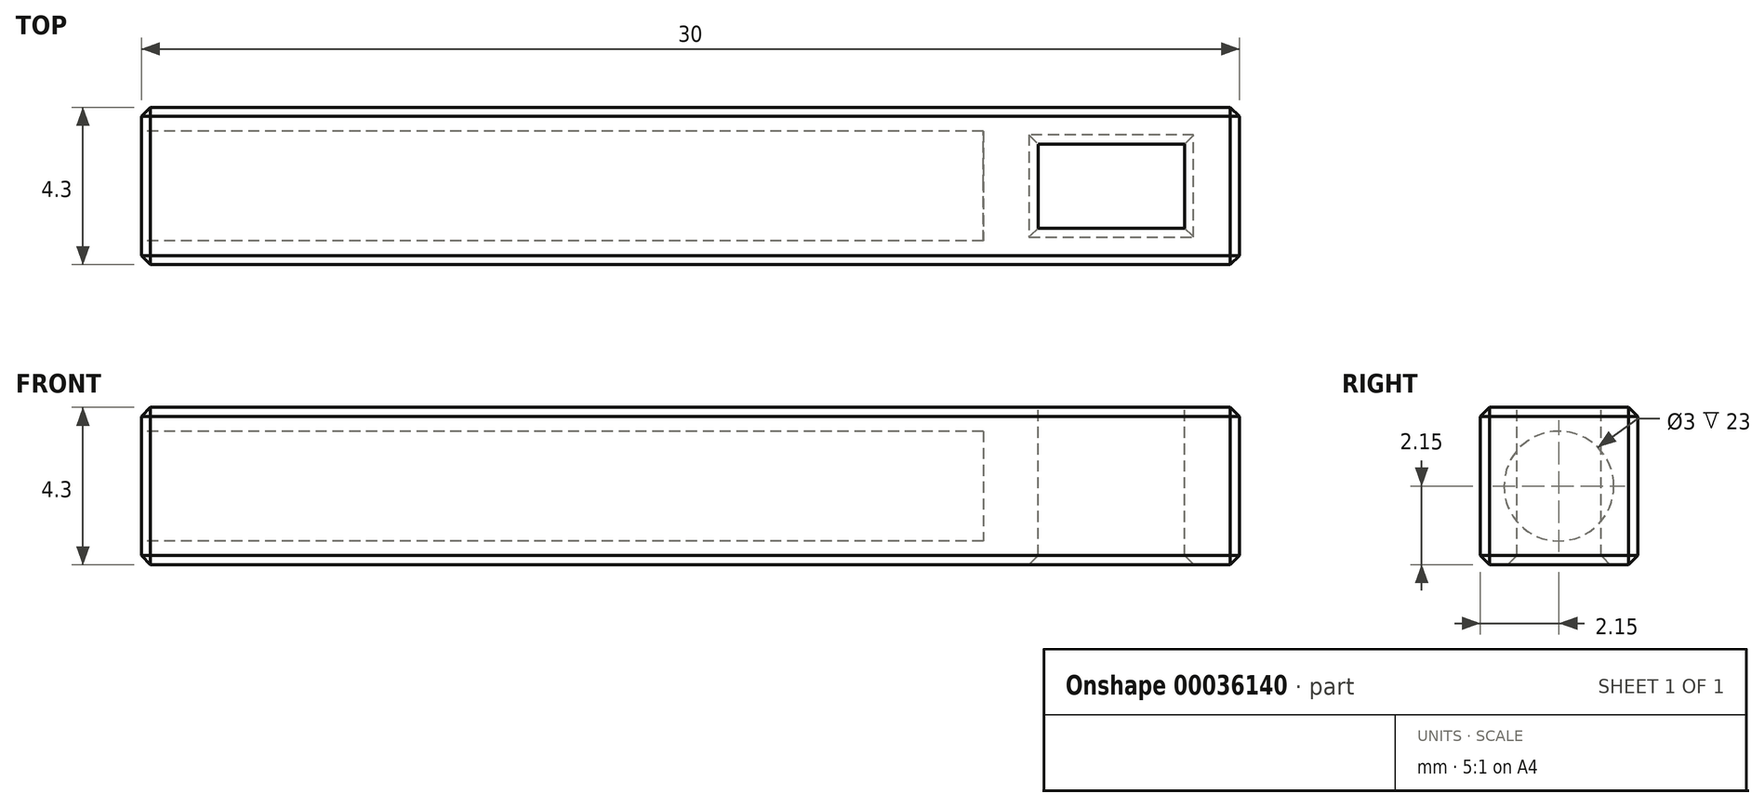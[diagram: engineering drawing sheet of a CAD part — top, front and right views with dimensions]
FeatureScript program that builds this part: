
annotation { "Feature Type Name" : "Feature", "Feature Type Description" : "" }
export const myFeature = defineFeature(function(context is Context, id is Id, definition is map)
    precondition{}
    {
        {
            var Q0;
            Q0=qCreatedBy(makeId("Top.planeOp"),FACE);
            var sketch = newSketch(context, id + "F0", { "sketchPlane" : qUnion([Q0])});
            skLineSegment(sketch, "E0.bottom", {"start": v(-16.76, 4.3) * mm, "end": v(13.24, 4.3) * mm});
            skLineSegment(sketch, "E0.top", {"start": v(-16.76, 0) * mm, "end": v(13.24, 0) * mm});
            skLineSegment(sketch, "E0.left", {"start": v(-16.76, 4.3) * mm, "end": v(-16.76, 0) * mm});
            skLineSegment(sketch, "E0.right", {"start": v(13.24, 4.3) * mm, "end": v(13.24, 0) * mm});
            skSolve(sketch);
        }
        {
            var Q0;
            Q0 = qSketchRegion(id + "F0", true);
            extrude(context, id + "F1", {"entities" : qUnion([Q0]), "depth" : 4.3 * mm});
        }
        {
            var Q0;
            Q0=makeQuery(id+"F1.opExtrude","CAP_FACE",FACE,{"disambiguationData":[OSD([sQuery(id+"F0.wireOp",EDGE,"E0.bottom"),sQuery(id+"F0.wireOp",EDGE,"E0.top"),sQuery(id+"F0.wireOp",EDGE,"E0.left"),sQuery(id+"F0.wireOp",EDGE,"E0.right")])],"isStart":false});
            var sketch = newSketch(context, id + "F2", { "sketchPlane" : qUnion([Q0])});
            skLineSegment(sketch, "E1.bottom", {"start": v(11.74, 3.3) * mm, "end": v(7.74, 3.3) * mm});
            skLineSegment(sketch, "E1.top", {"start": v(11.74, 1) * mm, "end": v(7.74, 1) * mm});
            skLineSegment(sketch, "E1.left", {"start": v(11.74, 3.3) * mm, "end": v(11.74, 1) * mm});
            skLineSegment(sketch, "E1.right", {"start": v(7.74, 3.3) * mm, "end": v(7.74, 1) * mm});
            skSolve(sketch);
        }
        {
            var Q0;
            Q0 = qSketchRegion(id + "F2", true);
            extrude(context, id + "F6", {"entities" : qUnion([Q0]), "operationType" : NewBodyOperationType.REMOVE, "endBound" : BoundingType.THROUGH_ALL, "oppositeDirection" : true, "depth" : 25 * mm});
        }
        {
            var Q0;
            Q0=makeQuery(id+"F1.opExtrude","CAP_EDGE",EDGE,{"disambiguationData":[OSD([sQuery(id+"F0.wireOp",EDGE,"E0.right")])],"isStart":false});
            var Q1;
            Q1=makeQuery(id+"F1.opExtrude","CAP_EDGE",EDGE,{"disambiguationData":[OSD([sQuery(id+"F0.wireOp",EDGE,"E0.top")])],"isStart":false});
            var Q2;
            Q2=makeQuery(id+"F1.opExtrude","CAP_EDGE",EDGE,{"disambiguationData":[OSD([sQuery(id+"F0.wireOp",EDGE,"E0.bottom")])],"isStart":false});
            var Q3;
            Q3=makeQuery(id+"F1.opExtrude","SWEPT_EDGE",EDGE,{"disambiguationData":[OSD([sQuery(id+"F0.wireOp",EDGE,"E0.top"),sQuery(id+"F0.wireOp",EDGE,"E0.right")])]});
            var Q4;
            Q4=makeQuery(id+"F1.opExtrude","SWEPT_EDGE",EDGE,{"disambiguationData":[OSD([sQuery(id+"F0.wireOp",EDGE,"E0.bottom"),sQuery(id+"F0.wireOp",EDGE,"E0.right")])]});
            var Q5;
            Q5=makeQuery(id+"F1.opExtrude","CAP_EDGE",EDGE,{"disambiguationData":[OSD([sQuery(id+"F0.wireOp",EDGE,"E0.bottom")])],"isStart":true});
            var Q6;
            Q6=makeQuery(id+"F1.opExtrude","CAP_EDGE",EDGE,{"disambiguationData":[OSD([sQuery(id+"F0.wireOp",EDGE,"E0.right")])],"isStart":true});
            var Q7;
            Q7=makeQuery(id+"F1.opExtrude","CAP_EDGE",EDGE,{"disambiguationData":[OSD([sQuery(id+"F0.wireOp",EDGE,"E0.top")])],"isStart":true});
            var Q8;
            Q8=makeQuery(id+"F6.boolean.opBoolean","INTERSECT",EDGE,{"derivedFrom":[makeQuery(id+"F1.opExtrude","CAP_FACE",FACE,{"disambiguationData":[OSD([sQuery(id+"F0.wireOp",EDGE,"E0.bottom"),sQuery(id+"F0.wireOp",EDGE,"E0.top"),sQuery(id+"F0.wireOp",EDGE,"E0.left"),sQuery(id+"F0.wireOp",EDGE,"E0.right")])],"isStart":true}),makeQuery(id+"F6.opExtrude","SWEPT_FACE",FACE,{"disambiguationData":[OSD([sQuery(id+"F2.wireOp",EDGE,"E1.bottom")])]})]});
            var Q9;
            Q9=makeQuery(id+"F6.boolean.opBoolean","INTERSECT",EDGE,{"derivedFrom":[makeQuery(id+"F1.opExtrude","CAP_FACE",FACE,{"disambiguationData":[OSD([sQuery(id+"F0.wireOp",EDGE,"E0.bottom"),sQuery(id+"F0.wireOp",EDGE,"E0.top"),sQuery(id+"F0.wireOp",EDGE,"E0.left"),sQuery(id+"F0.wireOp",EDGE,"E0.right")])],"isStart":true}),makeQuery(id+"F6.opExtrude","SWEPT_FACE",FACE,{"disambiguationData":[OSD([sQuery(id+"F2.wireOp",EDGE,"E1.right")])]})]});
            var Q10;
            Q10=makeQuery(id+"F6.boolean.opBoolean","INTERSECT",EDGE,{"derivedFrom":[makeQuery(id+"F1.opExtrude","CAP_FACE",FACE,{"disambiguationData":[OSD([sQuery(id+"F0.wireOp",EDGE,"E0.bottom"),sQuery(id+"F0.wireOp",EDGE,"E0.top"),sQuery(id+"F0.wireOp",EDGE,"E0.left"),sQuery(id+"F0.wireOp",EDGE,"E0.right")])],"isStart":true}),makeQuery(id+"F6.opExtrude","SWEPT_FACE",FACE,{"disambiguationData":[OSD([sQuery(id+"F2.wireOp",EDGE,"E1.top")])]})]});
            var Q11;
            Q11=makeQuery(id+"F6.boolean.opBoolean","INTERSECT",EDGE,{"derivedFrom":[makeQuery(id+"F1.opExtrude","CAP_FACE",FACE,{"disambiguationData":[OSD([sQuery(id+"F0.wireOp",EDGE,"E0.bottom"),sQuery(id+"F0.wireOp",EDGE,"E0.top"),sQuery(id+"F0.wireOp",EDGE,"E0.left"),sQuery(id+"F0.wireOp",EDGE,"E0.right")])],"isStart":true}),makeQuery(id+"F6.opExtrude","SWEPT_FACE",FACE,{"disambiguationData":[OSD([sQuery(id+"F2.wireOp",EDGE,"E1.left")])]})]});
            var Q12;
            Q12=makeQuery(id+"F6.boolean.opBoolean","COPY",EDGE,{"derivedFrom":makeQuery(id+"F6.opExtrude","CAP_EDGE",EDGE,{"disambiguationData":[OSD([sQuery(id+"F2.wireOp",EDGE,"E1.right")])],"isStart":true})});
            var Q13;
            Q13=makeQuery(id+"F6.boolean.opBoolean","COPY",EDGE,{"derivedFrom":makeQuery(id+"F6.opExtrude","CAP_EDGE",EDGE,{"disambiguationData":[OSD([sQuery(id+"F2.wireOp",EDGE,"E1.left")])],"isStart":true})});
            var Q14;
            Q14=makeQuery(id+"F6.boolean.opBoolean","COPY",EDGE,{"derivedFrom":makeQuery(id+"F6.opExtrude","CAP_EDGE",EDGE,{"disambiguationData":[OSD([sQuery(id+"F2.wireOp",EDGE,"E1.bottom")])],"isStart":true})});
            var Q15;
            Q15=makeQuery(id+"F6.boolean.opBoolean","COPY",EDGE,{"derivedFrom":makeQuery(id+"F6.opExtrude","CAP_EDGE",EDGE,{"disambiguationData":[OSD([sQuery(id+"F2.wireOp",EDGE,"E1.top")])],"isStart":true})});
            var Q16;
            Q16=makeQuery(id+"F1.opExtrude","CAP_EDGE",EDGE,{"disambiguationData":[OSD([sQuery(id+"F0.wireOp",EDGE,"E0.left")])],"isStart":false});
            var Q17;
            Q17=makeQuery(id+"F1.opExtrude","SWEPT_EDGE",EDGE,{"disambiguationData":[OSD([sQuery(id+"F0.wireOp",EDGE,"E0.top"),sQuery(id+"F0.wireOp",EDGE,"E0.left")])]});
            var Q18;
            Q18=makeQuery(id+"F1.opExtrude","CAP_EDGE",EDGE,{"disambiguationData":[OSD([sQuery(id+"F0.wireOp",EDGE,"E0.left")])],"isStart":true});
            var Q19;
            Q19=makeQuery(id+"F1.opExtrude","SWEPT_EDGE",EDGE,{"disambiguationData":[OSD([sQuery(id+"F0.wireOp",EDGE,"E0.bottom"),sQuery(id+"F0.wireOp",EDGE,"E0.left")])]});
            chamfer(context, id + "F3", {"entities" : qUnion([Q0, Q1, Q2, Q3, Q4, Q5, Q6, Q7, Q8, Q9, Q10, Q11, Q12, Q13, Q14, Q15, Q16, Q17, Q18, Q19]), "width" : .25 * mm, "tangentPropagation" : true});
        }
        {
            var Q0;
            Q0=makeQuery(id+"F1.opExtrude","SWEPT_FACE",FACE,{"disambiguationData":[OSD([sQuery(id+"F0.wireOp",EDGE,"E0.left")])]});
            var sketch = newSketch(context, id + "F4", { "sketchPlane" : qUnion([Q0])});
            skCircle(sketch, "E2", {"center": v(-2.15, 2.15) * mm, "radius": 1.5 * mm});
            skSolve(sketch);
        }
        {
            var Q0;
            Q0 = qSketchRegion(id + "F4", true);
            extrude(context, id + "F5", {"entities" : qUnion([Q0]), "operationType" : NewBodyOperationType.REMOVE, "oppositeDirection" : true, "depth" : 23 * mm});
        }
    });
